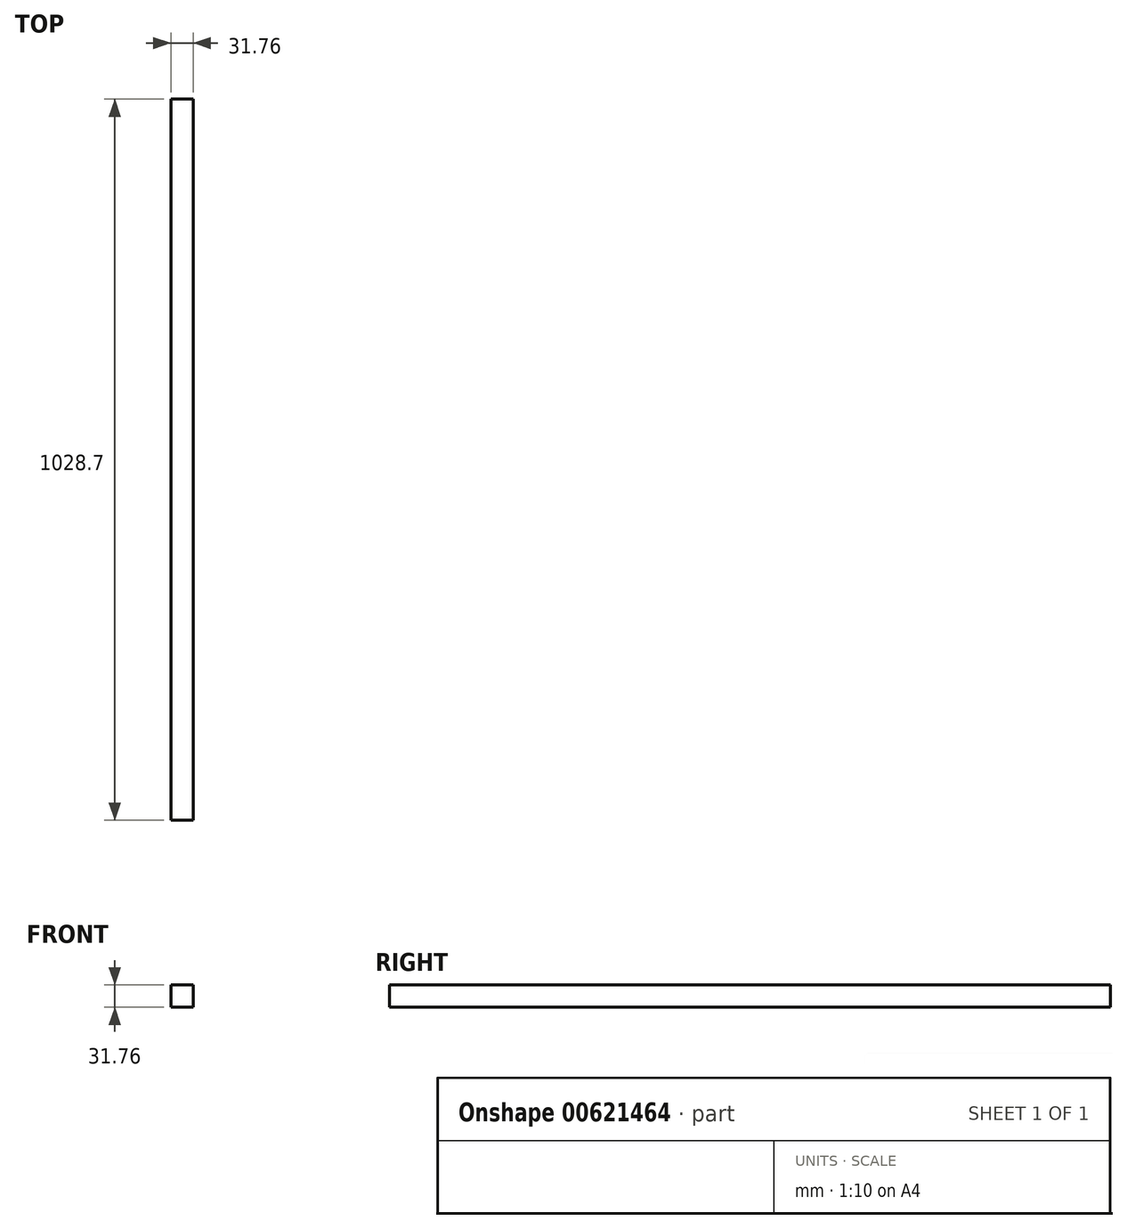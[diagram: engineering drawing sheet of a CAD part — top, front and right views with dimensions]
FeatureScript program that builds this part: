
annotation { "Feature Type Name" : "Feature", "Feature Type Description" : "" }
export const myFeature = defineFeature(function(context is Context, id is Id, definition is map)
    precondition{}
    {
        {
            var Q0;
            Q0=qCreatedBy(makeId("Front.planeOp"),FACE);
            var sketch = newSketch(context, id + "F0", { "sketchPlane" : qUnion([Q0])});
            skLineSegment(sketch, "E0.bottom", {"start": v(15.88, 15.87) * mm, "end": v(-15.88, 15.87) * mm});
            skLineSegment(sketch, "E0.top", {"start": v(15.88, -15.88) * mm, "end": v(-15.88, -15.88) * mm});
            skLineSegment(sketch, "E0.left", {"start": v(15.88, 15.87) * mm, "end": v(15.88, -15.88) * mm});
            skLineSegment(sketch, "E0.right", {"start": v(-15.88, 15.87) * mm, "end": v(-15.88, -15.88) * mm});
            skPoint(sketch, "E0.middle", {"position": v(0, 0) * mm});
            skSolve(sketch);
        }
        {
            var Q0;
            Q0 = qSketchRegion(id + "F0", true);
            extrude(context, id + "F1", {"entities" : qUnion([Q0]), "depth" : 1028.7 * mm, "offsetDistance" : 25.4 * mm});
        }
    });
